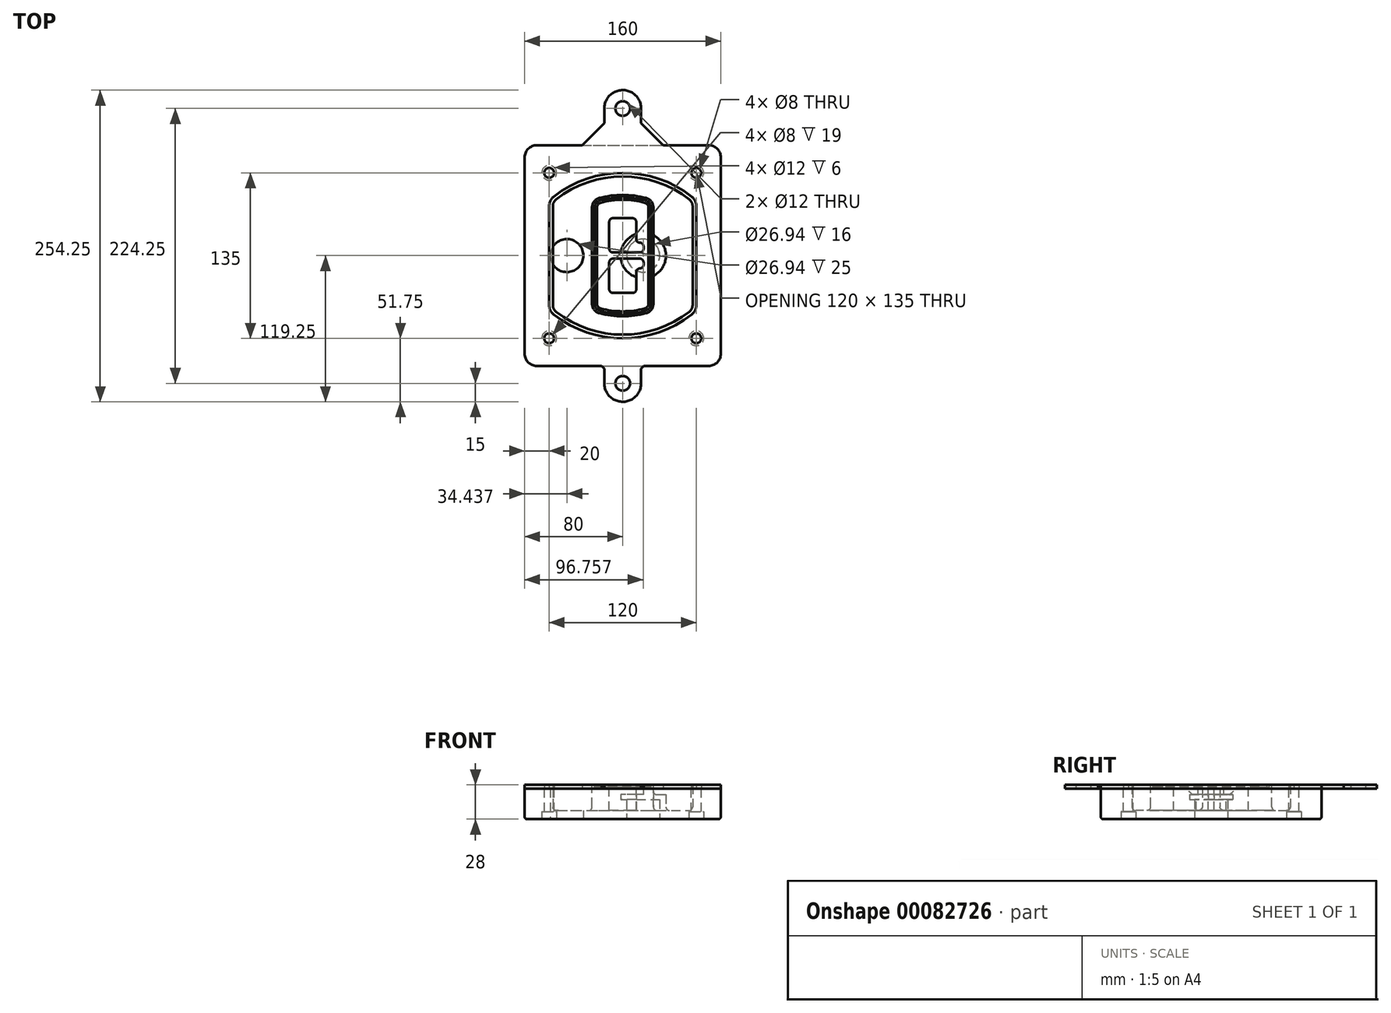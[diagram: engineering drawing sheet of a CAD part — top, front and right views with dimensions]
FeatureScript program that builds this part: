
annotation { "Feature Type Name" : "Feature", "Feature Type Description" : "" }
export const myFeature = defineFeature(function(context is Context, id is Id, definition is map)
    precondition{}
    {
        {
            var Q0;
            Q0=qCreatedBy(makeId("Top.planeOp"),FACE);
            var sketch = newSketch(context, id + "F0", { "sketchPlane" : qUnion([Q0])});
            skPoint(sketch, "E0.rect.middle", {"position": v(0, 0) * mm});
            skLineSegment(sketch, "E1.bottom", {"start": v(-70, -90) * mm, "end": v(70, -90) * mm});
            skLineSegment(sketch, "E1.top", {"start": v(-70, 90) * mm, "end": v(70, 90) * mm});
            skLineSegment(sketch, "E1.left", {"start": v(-80, -80) * mm, "end": v(-80, 80) * mm});
            skLineSegment(sketch, "E1.right", {"start": v(80, -80) * mm, "end": v(80, 80) * mm});
            skLineSegment(sketch, "E2", {"start": v(-80, 90) * mm, "end": v(80, -90) * mm, "construction": true});
            skLineSegment(sketch, "E3", {"start": v(80, 90) * mm, "end": v(-80, -90) * mm, "construction": true});
            skCircle(sketch, "E4", {"center": v(-60, 67.5) * mm, "radius": 4 * mm});
            skCircle(sketch, "E5", {"center": v(60, 67.5) * mm, "radius": 4 * mm});
            skCircle(sketch, "E6", {"center": v(60, -67.5) * mm, "radius": 4 * mm});
            skCircle(sketch, "E7", {"center": v(-60, -67.5) * mm, "radius": 4 * mm});
            skLineSegment(sketch, "E8", {"start": v(-60, 67.5) * mm, "end": v(60, 67.5) * mm, "construction": true});
            skLineSegment(sketch, "E9", {"start": v(60, 67.5) * mm, "end": v(60, -67.5) * mm, "construction": true});
            skLineSegment(sketch, "E10", {"start": v(60, -67.5) * mm, "end": v(-60, -67.5) * mm, "construction": true});
            skLineSegment(sketch, "E11", {"start": v(-60, -67.5) * mm, "end": v(-60, 67.5) * mm, "construction": true});
            skLineSegment(sketch, "E12", {"start": v(-60, 40.3) * mm, "end": v(-60, -40.3) * mm});
            skLineSegment(sketch, "E13", {"start": v(60, 40.3) * mm, "end": v(60, -40.3) * mm});
            skArc(sketch, "E14", {"start": v(56.15, 48.18) * mm, "mid": v(0, 67.5) * mm, "end": v(-56.15, 48.18) * mm});
            skArc(sketch, "E15", {"start": v(-56.15, -48.18) * mm, "mid": v(0, -67.5) * mm, "end": v(56.15, -48.18) * mm});
            skLineSegment(sketch, "E16", {"start": v(-60, 0) * mm, "end": v(60, 0) * mm, "construction": true});
            skPoint(sketch, "E17.visualSharp", {"position": v(-60, -45) * mm});
            skArc(sketch, "E17.filletArc", {"start": v(-60, -40.3) * mm, "mid": v(-58.99, -44.68) * mm, "end": v(-56.15, -48.18) * mm});
            skPoint(sketch, "E18.visualSharp", {"position": v(-60, 45) * mm});
            skArc(sketch, "E18.filletArc", {"start": v(-56.15, 48.18) * mm, "mid": v(-58.99, 44.68) * mm, "end": v(-60, 40.3) * mm});
            skPoint(sketch, "E19.visualSharp", {"position": v(60, 45) * mm});
            skArc(sketch, "E19.filletArc", {"start": v(60, 40.3) * mm, "mid": v(58.99, 44.68) * mm, "end": v(56.15, 48.18) * mm});
            skPoint(sketch, "E20.visualSharp", {"position": v(60, -45) * mm});
            skArc(sketch, "E20.filletArc", {"start": v(56.15, -48.18) * mm, "mid": v(58.99, -44.68) * mm, "end": v(60, -40.3) * mm});
            skPoint(sketch, "E21.visualSharp", {"position": v(-80, 90) * mm});
            skArc(sketch, "E21.filletArc", {"start": v(-70, 90) * mm, "mid": v(-77.07, 87.07) * mm, "end": v(-80, 80) * mm});
            skPoint(sketch, "E22.visualSharp", {"position": v(80, 90) * mm});
            skArc(sketch, "E22.filletArc", {"start": v(80, 80) * mm, "mid": v(77.07, 87.07) * mm, "end": v(70, 90) * mm});
            skPoint(sketch, "E23.visualSharp", {"position": v(80, -90) * mm});
            skArc(sketch, "E23.filletArc", {"start": v(70, -90) * mm, "mid": v(77.07, -87.07) * mm, "end": v(80, -80) * mm});
            skPoint(sketch, "E24.visualSharp", {"position": v(-80, -90) * mm});
            skArc(sketch, "E24.filletArc", {"start": v(-80, -80) * mm, "mid": v(-77.07, -87.07) * mm, "end": v(-70, -90) * mm});
            skArc(sketch, "E25.0", {"start": v(57, 40.3) * mm, "mid": v(56.3, 43.36) * mm, "end": v(54.3, 45.81) * mm});
            skLineSegment(sketch, "E25.1", {"start": v(57, 40.3) * mm, "end": v(57, -40.3) * mm});
            skArc(sketch, "E25.2", {"start": v(54.3, -45.81) * mm, "mid": v(56.3, -43.36) * mm, "end": v(57, -40.3) * mm});
            skArc(sketch, "E25.3", {"start": v(-54.3, -45.81) * mm, "mid": v(0, -64.5) * mm, "end": v(54.3, -45.81) * mm});
            skArc(sketch, "E25.4", {"start": v(-57, -40.3) * mm, "mid": v(-56.3, -43.36) * mm, "end": v(-54.3, -45.81) * mm});
            skArc(sketch, "E25.5", {"start": v(54.3, 45.81) * mm, "mid": v(0, 64.5) * mm, "end": v(-54.3, 45.81) * mm});
            skLineSegment(sketch, "E25.6", {"start": v(-57, 40.3) * mm, "end": v(-57, -40.3) * mm});
            skArc(sketch, "E25.7", {"start": v(-54.3, 45.81) * mm, "mid": v(-56.3, 43.36) * mm, "end": v(-57, 40.3) * mm});
            skArc(sketch, "E26.0", {"start": v(-58.62, 51.33) * mm, "mid": v(-62.58, 46.43) * mm, "end": v(-64, 40.3) * mm});
            skArc(sketch, "E26.1", {"start": v(58.62, 51.33) * mm, "mid": v(0, 71.5) * mm, "end": v(-58.62, 51.33) * mm});
            skArc(sketch, "E26.2", {"start": v(64, 40.3) * mm, "mid": v(62.58, 46.43) * mm, "end": v(58.62, 51.33) * mm});
            skLineSegment(sketch, "E26.3", {"start": v(64, 40.3) * mm, "end": v(64, -40.3) * mm});
            skArc(sketch, "E26.4", {"start": v(58.62, -51.33) * mm, "mid": v(62.58, -46.43) * mm, "end": v(64, -40.3) * mm});
            skLineSegment(sketch, "E26.5", {"start": v(-64, 40.3) * mm, "end": v(-64, -40.3) * mm});
            skArc(sketch, "E26.6", {"start": v(-58.62, -51.33) * mm, "mid": v(0, -71.5) * mm, "end": v(58.62, -51.33) * mm});
            skArc(sketch, "E26.7", {"start": v(-64, -40.3) * mm, "mid": v(-62.58, -46.43) * mm, "end": v(-58.62, -51.33) * mm});
            skSolve(sketch);
        }
        {
            var Q0;
            Q0=makeQuery(id+"F0.imprint","IMPRINT",FACE,{"disambiguationData":[TD([[makeQuery(id+"F0.imprint","IMPRINT",EDGE,{"derivedFrom":sQuery(id+"F0.wireOp",EDGE,"E1.bottom")}),1.0]])]});
            var Q1;
            Q1=makeQuery(id+"F0.imprint","IMPRINT",FACE,{"disambiguationData":[TD([[makeQuery(id+"F0.imprint","IMPRINT",EDGE,{"derivedFrom":sQuery(id+"F0.wireOp",EDGE,"E12")}),1.0]])]});
            var Q2;
            Q2=makeQuery(id+"F0.imprint","IMPRINT",FACE,{"disambiguationData":[TD([[makeQuery(id+"F0.imprint","IMPRINT",EDGE,{"derivedFrom":sQuery(id+"F0.wireOp",EDGE,"E25.0")}),1.0]])]});
            var Q3;
            Q3=makeQuery(id+"F0.imprint","IMPRINT",FACE,{"disambiguationData":[TD([[makeQuery(id+"F0.imprint","IMPRINT",EDGE,{"derivedFrom":sQuery(id+"F0.wireOp",EDGE,"E12")}),-1.0]])]});
            extrude(context, id + "F1", {"entities" : qUnion([Q0, Q1, Q2, Q3]), "oppositeDirection" : true, "depth" : 25 * mm});
        }
        {
            var Q0;
            Q0=makeQuery(id+"F0.imprint","IMPRINT",FACE,{"disambiguationData":[TD([[makeQuery(id+"F0.imprint","IMPRINT",EDGE,{"derivedFrom":sQuery(id+"F0.wireOp",EDGE,"E12")}),1.0]])]});
            extrude(context, id + "F2", {"entities" : qUnion([Q0]), "operationType" : NewBodyOperationType.ADD, "depth" : 3 * mm});
        }
        {
            var Q0;
            Q0=makeQuery(id+"F0.imprint","IMPRINT",FACE,{"disambiguationData":[TD([[makeQuery(id+"F0.imprint","IMPRINT",EDGE,{"derivedFrom":sQuery(id+"F0.wireOp",EDGE,"E25.0")}),1.0]])]});
            extrude(context, id + "F3", {"entities" : qUnion([Q0]), "operationType" : NewBodyOperationType.REMOVE, "oppositeDirection" : true, "depth" : 18 * mm});
        }
        {
            var Q0;
            Q0=makeQuery(id+"F2.opExtrude","CAP_FACE",FACE,{"disambiguationData":[OSD([sQuery(id+"F0.wireOp",EDGE,"E12"),sQuery(id+"F0.wireOp",EDGE,"E13"),sQuery(id+"F0.wireOp",EDGE,"E14"),sQuery(id+"F0.wireOp",EDGE,"E15"),sQuery(id+"F0.wireOp",EDGE,"E17.filletArc"),sQuery(id+"F0.wireOp",EDGE,"E18.filletArc"),sQuery(id+"F0.wireOp",EDGE,"E19.filletArc"),sQuery(id+"F0.wireOp",EDGE,"E20.filletArc"),sQuery(id+"F0.wireOp",EDGE,"E25.0"),sQuery(id+"F0.wireOp",EDGE,"E25.1"),sQuery(id+"F0.wireOp",EDGE,"E25.2"),sQuery(id+"F0.wireOp",EDGE,"E25.3"),sQuery(id+"F0.wireOp",EDGE,"E25.4"),sQuery(id+"F0.wireOp",EDGE,"E25.5"),sQuery(id+"F0.wireOp",EDGE,"E25.6"),sQuery(id+"F0.wireOp",EDGE,"E25.7")])],"isStart":false});
            var sketch = newSketch(context, id + "F4", { "sketchPlane" : qUnion([Q0])});
            skArc(sketch, "E27.0", {"start": v(-19.08, -46.97) * mm, "mid": v(0, -49.5) * mm, "end": v(19.08, -46.97) * mm});
            skArc(sketch, "E28.0", {"start": v(19.08, 46.97) * mm, "mid": v(0, 49.5) * mm, "end": v(-19.08, 46.97) * mm});
            skLineSegment(sketch, "E29", {"start": v(-25, 39.25) * mm, "end": v(-25, -39.25) * mm});
            skLineSegment(sketch, "E30", {"start": v(25, 39.25) * mm, "end": v(25, -39.25) * mm});
            skLineSegment(sketch, "E31", {"start": v(-25, 45.1) * mm, "end": v(25, 45.1) * mm, "construction": true});
            skLineSegment(sketch, "E32", {"start": v(-25, -45.1) * mm, "end": v(25, -45.1) * mm, "construction": true});
            skPoint(sketch, "E33.visualSharp", {"position": v(-25, 45.1) * mm});
            skArc(sketch, "E33.filletArc", {"start": v(-19.08, 46.97) * mm, "mid": v(-23.35, 44.11) * mm, "end": v(-25, 39.25) * mm});
            skPoint(sketch, "E34.visualSharp", {"position": v(25, 45.1) * mm});
            skArc(sketch, "E34.filletArc", {"start": v(25, 39.25) * mm, "mid": v(23.35, 44.11) * mm, "end": v(19.08, 46.97) * mm});
            skPoint(sketch, "E35.visualSharp", {"position": v(25, -45.1) * mm});
            skArc(sketch, "E35.filletArc", {"start": v(19.08, -46.97) * mm, "mid": v(23.35, -44.11) * mm, "end": v(25, -39.25) * mm});
            skPoint(sketch, "E36.visualSharp", {"position": v(-25, -45.1) * mm});
            skArc(sketch, "E36.filletArc", {"start": v(-25, -39.25) * mm, "mid": v(-23.35, -44.11) * mm, "end": v(-19.08, -46.97) * mm});
            skArc(sketch, "E37.0", {"start": v(54.3, 45.81) * mm, "mid": v(0, 64.5) * mm, "end": v(-54.3, 45.81) * mm});
            skArc(sketch, "E37.1", {"start": v(-54.3, 45.81) * mm, "mid": v(-56.3, 43.36) * mm, "end": v(-57, 40.3) * mm});
            skLineSegment(sketch, "E37.2", {"start": v(-57, 40.3) * mm, "end": v(-57, -40.3) * mm});
            skArc(sketch, "E37.3", {"start": v(-57, -40.3) * mm, "mid": v(-56.3, -43.36) * mm, "end": v(-54.3, -45.81) * mm});
            skArc(sketch, "E37.4", {"start": v(-54.3, -45.81) * mm, "mid": v(0, -64.5) * mm, "end": v(54.3, -45.81) * mm});
            skArc(sketch, "E37.5", {"start": v(54.3, -45.81) * mm, "mid": v(56.3, -43.36) * mm, "end": v(57, -40.3) * mm});
            skLineSegment(sketch, "E37.6", {"start": v(57, 40.3) * mm, "end": v(57, -40.3) * mm});
            skArc(sketch, "E37.7", {"start": v(57, 40.3) * mm, "mid": v(56.3, 43.36) * mm, "end": v(54.3, 45.81) * mm});
            skLineSegment(sketch, "E38.0", {"start": v(23, 39.25) * mm, "end": v(23, -39.25) * mm});
            skArc(sketch, "E38.1", {"start": v(18.56, -45.04) * mm, "mid": v(21.76, -42.9) * mm, "end": v(23, -39.25) * mm});
            skArc(sketch, "E38.2", {"start": v(-18.56, -45.04) * mm, "mid": v(0, -47.5) * mm, "end": v(18.56, -45.04) * mm});
            skArc(sketch, "E38.3", {"start": v(-23, -39.25) * mm, "mid": v(-21.76, -42.9) * mm, "end": v(-18.56, -45.04) * mm});
            skLineSegment(sketch, "E38.4", {"start": v(-23, 39.25) * mm, "end": v(-23, -39.25) * mm});
            skArc(sketch, "E38.5", {"start": v(23, 39.25) * mm, "mid": v(21.76, 42.9) * mm, "end": v(18.56, 45.04) * mm});
            skArc(sketch, "E38.6", {"start": v(-18.56, 45.04) * mm, "mid": v(-21.76, 42.9) * mm, "end": v(-23, 39.25) * mm});
            skArc(sketch, "E38.7", {"start": v(18.56, 45.04) * mm, "mid": v(0, 47.5) * mm, "end": v(-18.56, 45.04) * mm});
            skArc(sketch, "E39.0", {"start": v(21, 39.25) * mm, "mid": v(20.18, 41.68) * mm, "end": v(18.04, 43.1) * mm});
            skLineSegment(sketch, "E39.1", {"start": v(21, 39.25) * mm, "end": v(21, -39.25) * mm});
            skArc(sketch, "E39.2", {"start": v(18.04, -43.1) * mm, "mid": v(20.18, -41.68) * mm, "end": v(21, -39.25) * mm});
            skArc(sketch, "E39.3", {"start": v(-18.04, -43.1) * mm, "mid": v(0, -45.5) * mm, "end": v(18.04, -43.1) * mm});
            skArc(sketch, "E39.4", {"start": v(-21, -39.25) * mm, "mid": v(-20.18, -41.68) * mm, "end": v(-18.04, -43.1) * mm});
            skArc(sketch, "E39.5", {"start": v(18.04, 43.1) * mm, "mid": v(0, 45.5) * mm, "end": v(-18.04, 43.1) * mm});
            skLineSegment(sketch, "E39.6", {"start": v(-21, 39.25) * mm, "end": v(-21, -39.25) * mm});
            skArc(sketch, "E39.7", {"start": v(-18.04, 43.1) * mm, "mid": v(-20.18, 41.68) * mm, "end": v(-21, 39.25) * mm});
            skLineSegment(sketch, "E40", {"start": v(-25, 0) * mm, "end": v(25, 0) * mm, "construction": true});
            skLineSegment(sketch, "E41", {"start": v(-11, 5.5) * mm, "end": v(-11, 27.5) * mm});
            skLineSegment(sketch, "E42", {"start": v(-8, 30.5) * mm, "end": v(8, 30.5) * mm});
            skLineSegment(sketch, "E43", {"start": v(11, 27.5) * mm, "end": v(11, 13.5) * mm});
            skLineSegment(sketch, "E44", {"start": v(14, 10.5) * mm, "end": v(14, 10.5) * mm});
            skLineSegment(sketch, "E45", {"start": v(17, 7.5) * mm, "end": v(17, 5.5) * mm});
            skLineSegment(sketch, "E46", {"start": v(14, 2.5) * mm, "end": v(-8, 2.5) * mm});
            skPoint(sketch, "E47.visualSharp", {"position": v(-11, 30.5) * mm});
            skArc(sketch, "E47.filletArc", {"start": v(-8, 30.5) * mm, "mid": v(-10.12, 29.62) * mm, "end": v(-11, 27.5) * mm});
            skPoint(sketch, "E48.visualSharp", {"position": v(11, 30.5) * mm});
            skArc(sketch, "E48.filletArc", {"start": v(11, 27.5) * mm, "mid": v(10.12, 29.62) * mm, "end": v(8, 30.5) * mm});
            skPoint(sketch, "E49.visualSharp", {"position": v(11, 10.5) * mm});
            skArc(sketch, "E49.filletArc", {"start": v(11, 13.5) * mm, "mid": v(11.88, 11.38) * mm, "end": v(14, 10.5) * mm});
            skPoint(sketch, "E50.visualSharp", {"position": v(17, 10.5) * mm});
            skArc(sketch, "E50.filletArc", {"start": v(17, 7.5) * mm, "mid": v(16.12, 9.62) * mm, "end": v(14, 10.5) * mm});
            skPoint(sketch, "E51.visualSharp", {"position": v(17, 2.5) * mm});
            skArc(sketch, "E51.filletArc", {"start": v(14, 2.5) * mm, "mid": v(16.12, 3.38) * mm, "end": v(17, 5.5) * mm});
            skPoint(sketch, "E52.visualSharp", {"position": v(-11, 2.5) * mm});
            skArc(sketch, "E52.filletArc", {"start": v(-11, 5.5) * mm, "mid": v(-10.12, 3.38) * mm, "end": v(-8, 2.5) * mm});
            skLineSegment(sketch, "E53.0.MirrorCS", {"start": v(14, -2.5) * mm, "end": v(-8, -2.5) * mm});
            skArc(sketch, "E54.0.MirrorCS", {"start": v(-11, -5.5) * mm, "mid": v(-10.12, -3.38) * mm, "end": v(-8, -2.5) * mm});
            skLineSegment(sketch, "E55.0.MirrorCS", {"start": v(-11, -5.5) * mm, "end": v(-11, -27.5) * mm});
            skArc(sketch, "E56.0.MirrorCS", {"start": v(-8, -30.5) * mm, "mid": v(-10.12, -29.62) * mm, "end": v(-11, -27.5) * mm});
            skLineSegment(sketch, "E57.0.MirrorCS", {"start": v(-8, -30.5) * mm, "end": v(8, -30.5) * mm});
            skArc(sketch, "E58.0.MirrorCS", {"start": v(11, -27.5) * mm, "mid": v(10.12, -29.62) * mm, "end": v(8, -30.5) * mm});
            skLineSegment(sketch, "E59.0.MirrorCS", {"start": v(11, -27.5) * mm, "end": v(11, -13.5) * mm});
            skArc(sketch, "E60.0.MirrorCS", {"start": v(11, -13.5) * mm, "mid": v(11.88, -11.38) * mm, "end": v(14, -10.5) * mm});
            skArc(sketch, "E61.0.MirrorCS", {"start": v(17, -7.5) * mm, "mid": v(16.12, -9.62) * mm, "end": v(14, -10.5) * mm});
            skLineSegment(sketch, "E62.0.MirrorCS", {"start": v(17, -7.5) * mm, "end": v(17, -5.5) * mm});
            skArc(sketch, "E63.0.MirrorCS", {"start": v(14, -2.5) * mm, "mid": v(16.12, -3.38) * mm, "end": v(17, -5.5) * mm});
            skSolve(sketch);
        }
        {
            var Q0;
            Q0=makeQuery(id+"F4.imprint","IMPRINT",FACE,{"disambiguationData":[TD([[makeQuery(id+"F4.imprint","IMPRINT",EDGE,{"derivedFrom":sQuery(id+"F4.wireOp",EDGE,"E27.0")}),1.0]])]});
            var Q1;
            Q1=makeQuery(id+"F4.imprint","IMPRINT",FACE,{"disambiguationData":[TD([[makeQuery(id+"F4.imprint","IMPRINT",EDGE,{"derivedFrom":sQuery(id+"F4.wireOp",EDGE,"E38.0")}),-1.0]])]});
            var Q2;
            Q2=makeQuery(id+"F4.imprint","IMPRINT",FACE,{"disambiguationData":[TD([[makeQuery(id+"F4.imprint","IMPRINT",EDGE,{"derivedFrom":sQuery(id+"F4.wireOp",EDGE,"E39.0")}),1.0]])]});
            extrude(context, id + "F5", {"entities" : qUnion([Q0, Q1, Q2]), "operationType" : NewBodyOperationType.ADD, "endBound" : BoundingType.UP_TO_NEXT, "oppositeDirection" : true, "depth" : 25 * mm});
        }
        {
            var Q0;
            Q0=makeQuery(id+"F4.imprint","IMPRINT",FACE,{"disambiguationData":[TD([[makeQuery(id+"F4.imprint","IMPRINT",EDGE,{"derivedFrom":sQuery(id+"F4.wireOp",EDGE,"E38.0")}),-1.0]])]});
            extrude(context, id + "F6", {"entities" : qUnion([Q0]), "operationType" : NewBodyOperationType.REMOVE, "oppositeDirection" : true, "depth" : 2 * mm});
        }
        {
            var Q0;
            Q0=makeQuery(id+"F1.opExtrude","CAP_FACE",FACE,{"disambiguationData":[OSD([sQuery(id+"F0.wireOp",EDGE,"E1.bottom"),sQuery(id+"F0.wireOp",EDGE,"E1.top"),sQuery(id+"F0.wireOp",EDGE,"E1.left"),sQuery(id+"F0.wireOp",EDGE,"E1.right"),sQuery(id+"F0.wireOp",EDGE,"E4"),sQuery(id+"F0.wireOp",EDGE,"E5"),sQuery(id+"F0.wireOp",EDGE,"E6"),sQuery(id+"F0.wireOp",EDGE,"E7"),sQuery(id+"F0.wireOp",EDGE,"E21.filletArc"),sQuery(id+"F0.wireOp",EDGE,"E22.filletArc"),sQuery(id+"F0.wireOp",EDGE,"E23.filletArc"),sQuery(id+"F0.wireOp",EDGE,"E24.filletArc")])],"isStart":false});
            var sketch = newSketch(context, id + "F7", { "sketchPlane" : qUnion([Q0])});
            skCircle(sketch, "E64", {"center": v(16.76, 0) * mm, "radius": 13.47 * mm});
            skCircle(sketch, "E65", {"center": v(-45.56, 0) * mm, "radius": 13.47 * mm});
            skLineSegment(sketch, "E66", {"start": v(80, 0) * mm, "end": v(-80, 0) * mm});
            skCircle(sketch, "E67", {"center": v(16.76, 0) * mm, "radius": 18.47 * mm});
            skCircle(sketch, "E68", {"center": v(60, -67.5) * mm, "radius": 6 * mm});
            skCircle(sketch, "E69", {"center": v(-60, -67.5) * mm, "radius": 6 * mm});
            skCircle(sketch, "E70", {"center": v(-60, 67.5) * mm, "radius": 6 * mm});
            skCircle(sketch, "E71", {"center": v(60, 67.5) * mm, "radius": 6 * mm});
            skSolve(sketch);
        }
        {
            var Q0;
            {var subQ1=sQuery(id+"F7.wireOp",EDGE,"E66");var subQ4=sQuery(id+"F7.wireOp",EDGE,"E64");var subQ6=makeQuery(id+"F7.imprint","INTERSECT",VERTEX,{"disambiguationData":[OD(0.0)],"derivedFrom":[subQ4,subQ1]});Q0=makeQuery(id+"F7.imprint","IMPRINT",FACE,{"disambiguationData":[TD([[makeQuery(id+"F7.imprint","IMPRINT",EDGE,{"disambiguationData":[TD([[subQ6,-1.0]])],"derivedFrom":subQ4}),-1.0]])]});}
            var Q1;
            {var subQ0=sQuery(id+"F7.wireOp",EDGE,"E66");var subQ1=sQuery(id+"F7.wireOp",EDGE,"E64");var subQ3=makeQuery(id+"F7.imprint","INTERSECT",VERTEX,{"disambiguationData":[OD(0.0)],"derivedFrom":[subQ1,subQ0]});Q1=makeQuery(id+"F7.imprint","IMPRINT",FACE,{"disambiguationData":[TD([[makeQuery(id+"F7.imprint","IMPRINT",EDGE,{"disambiguationData":[TD([[subQ3,-1.0]])],"derivedFrom":subQ1}),1.0]])]});}
            var Q2;
            {var subQ0=sQuery(id+"F7.wireOp",EDGE,"E66");var subQ1=sQuery(id+"F7.wireOp",EDGE,"E64");var subQ3=makeQuery(id+"F7.imprint","INTERSECT",VERTEX,{"disambiguationData":[OD(0.0)],"derivedFrom":[subQ1,subQ0]});Q2=makeQuery(id+"F7.imprint","IMPRINT",FACE,{"disambiguationData":[TD([[makeQuery(id+"F7.imprint","IMPRINT",EDGE,{"disambiguationData":[TD([[subQ3,1.0]])],"derivedFrom":subQ1}),1.0]])]});}
            var Q3;
            {var subQ1=sQuery(id+"F7.wireOp",EDGE,"E66");var subQ4=sQuery(id+"F7.wireOp",EDGE,"E64");var subQ6=makeQuery(id+"F7.imprint","INTERSECT",VERTEX,{"disambiguationData":[OD(0.0)],"derivedFrom":[subQ4,subQ1]});Q3=makeQuery(id+"F7.imprint","IMPRINT",FACE,{"disambiguationData":[TD([[makeQuery(id+"F7.imprint","IMPRINT",EDGE,{"disambiguationData":[TD([[subQ6,1.0]])],"derivedFrom":subQ4}),-1.0]])]});}
            extrude(context, id + "F8", {"entities" : qUnion([Q0, Q1, Q2, Q3]), "operationType" : NewBodyOperationType.ADD, "oppositeDirection" : true, "depth" : 20 * mm});
        }
        {
            var Q0;
            {var subQ0=sQuery(id+"F7.wireOp",EDGE,"E66");var subQ1=sQuery(id+"F7.wireOp",EDGE,"E64");var subQ3=makeQuery(id+"F7.imprint","INTERSECT",VERTEX,{"disambiguationData":[OD(0.0)],"derivedFrom":[subQ1,subQ0]});Q0=makeQuery(id+"F7.imprint","IMPRINT",FACE,{"disambiguationData":[TD([[makeQuery(id+"F7.imprint","IMPRINT",EDGE,{"disambiguationData":[TD([[subQ3,-1.0]])],"derivedFrom":subQ1}),1.0]])]});}
            var Q1;
            {var subQ0=sQuery(id+"F7.wireOp",EDGE,"E66");var subQ1=sQuery(id+"F7.wireOp",EDGE,"E64");var subQ3=makeQuery(id+"F7.imprint","INTERSECT",VERTEX,{"disambiguationData":[OD(0.0)],"derivedFrom":[subQ1,subQ0]});Q1=makeQuery(id+"F7.imprint","IMPRINT",FACE,{"disambiguationData":[TD([[makeQuery(id+"F7.imprint","IMPRINT",EDGE,{"disambiguationData":[TD([[subQ3,1.0]])],"derivedFrom":subQ1}),1.0]])]});}
            extrude(context, id + "F9", {"entities" : qUnion([Q0, Q1]), "operationType" : NewBodyOperationType.REMOVE, "oppositeDirection" : true, "depth" : 16 * mm});
        }
        {
            var Q0;
            {var subQ0=sQuery(id+"F7.wireOp",EDGE,"E66");var subQ1=sQuery(id+"F7.wireOp",EDGE,"E65");var subQ3=makeQuery(id+"F7.imprint","INTERSECT",VERTEX,{"disambiguationData":[OD(0.0)],"derivedFrom":[subQ1,subQ0]});Q0=makeQuery(id+"F7.imprint","IMPRINT",FACE,{"disambiguationData":[TD([[makeQuery(id+"F7.imprint","IMPRINT",EDGE,{"disambiguationData":[TD([[subQ3,-1.0]])],"derivedFrom":subQ1}),1.0]])]});}
            var Q1;
            {var subQ0=sQuery(id+"F7.wireOp",EDGE,"E66");var subQ1=sQuery(id+"F7.wireOp",EDGE,"E65");var subQ3=makeQuery(id+"F7.imprint","INTERSECT",VERTEX,{"disambiguationData":[OD(0.0)],"derivedFrom":[subQ1,subQ0]});Q1=makeQuery(id+"F7.imprint","IMPRINT",FACE,{"disambiguationData":[TD([[makeQuery(id+"F7.imprint","IMPRINT",EDGE,{"disambiguationData":[TD([[subQ3,1.0]])],"derivedFrom":subQ1}),1.0]])]});}
            extrude(context, id + "F10", {"entities" : qUnion([Q0, Q1]), "operationType" : NewBodyOperationType.REMOVE, "oppositeDirection" : true, "depth" : 25 * mm});
        }
        {
            var Q0;
            Q0=makeQuery(id+"F7.imprint","IMPRINT",FACE,{"disambiguationData":[TD([[makeQuery(id+"F7.imprint","IMPRINT",EDGE,{"derivedFrom":sQuery(id+"F7.wireOp",EDGE,"E68")}),1.0]])]});
            var Q1;
            Q1=makeQuery(id+"F7.imprint","IMPRINT",FACE,{"disambiguationData":[TD([[makeQuery(id+"F7.imprint","IMPRINT",EDGE,{"derivedFrom":makeQuery(id+"F1.opExtrude","CAP_EDGE",EDGE,{"disambiguationData":[OSD([sQuery(id+"F0.wireOp",EDGE,"E5")])],"isStart":false})}),-1.0]])]});
            var Q2;
            Q2=makeQuery(id+"F7.imprint","IMPRINT",FACE,{"disambiguationData":[TD([[makeQuery(id+"F7.imprint","IMPRINT",EDGE,{"derivedFrom":sQuery(id+"F7.wireOp",EDGE,"E69")}),1.0]])]});
            var Q3;
            Q3=makeQuery(id+"F7.imprint","IMPRINT",FACE,{"disambiguationData":[TD([[makeQuery(id+"F7.imprint","IMPRINT",EDGE,{"derivedFrom":makeQuery(id+"F1.opExtrude","CAP_EDGE",EDGE,{"disambiguationData":[OSD([sQuery(id+"F0.wireOp",EDGE,"E4")])],"isStart":false})}),-1.0]])]});
            var Q4;
            Q4=makeQuery(id+"F7.imprint","IMPRINT",FACE,{"disambiguationData":[TD([[makeQuery(id+"F7.imprint","IMPRINT",EDGE,{"derivedFrom":sQuery(id+"F7.wireOp",EDGE,"E70")}),1.0]])]});
            var Q5;
            Q5=makeQuery(id+"F7.imprint","IMPRINT",FACE,{"disambiguationData":[TD([[makeQuery(id+"F7.imprint","IMPRINT",EDGE,{"derivedFrom":makeQuery(id+"F1.opExtrude","CAP_EDGE",EDGE,{"disambiguationData":[OSD([sQuery(id+"F0.wireOp",EDGE,"E7")])],"isStart":false})}),-1.0]])]});
            var Q6;
            Q6=makeQuery(id+"F7.imprint","IMPRINT",FACE,{"disambiguationData":[TD([[makeQuery(id+"F7.imprint","IMPRINT",EDGE,{"derivedFrom":sQuery(id+"F7.wireOp",EDGE,"E71")}),1.0]])]});
            var Q7;
            Q7=makeQuery(id+"F7.imprint","IMPRINT",FACE,{"disambiguationData":[TD([[makeQuery(id+"F7.imprint","IMPRINT",EDGE,{"derivedFrom":makeQuery(id+"F1.opExtrude","CAP_EDGE",EDGE,{"disambiguationData":[OSD([sQuery(id+"F0.wireOp",EDGE,"E6")])],"isStart":false})}),-1.0]])]});
            extrude(context, id + "F11", {"entities" : qUnion([Q0, Q1, Q2, Q3, Q4, Q5, Q6, Q7]), "operationType" : NewBodyOperationType.REMOVE, "oppositeDirection" : true, "depth" : 6 * mm});
        }
        {
            var Q0;
            Q0=makeQuery(id+"F9.boolean.opBoolean","COPY",FACE,{"derivedFrom":makeQuery(id+"F9.opExtrude","CAP_FACE",FACE,{"disambiguationData":[OSD([sQuery(id+"F7.wireOp",EDGE,"E64")])],"isStart":false})});
            var sketch = newSketch(context, id + "F12", { "sketchPlane" : qUnion([Q0])});
            skArc(sketch, "E72.0", {"start": v(11, 17.55) * mm, "mid": v(2.57, 11.82) * mm, "end": v(-1.54, 2.5) * mm});
            skArc(sketch, "E72.1", {"start": v(-1.54, -2.5) * mm, "mid": v(2.57, -11.82) * mm, "end": v(11, -17.55) * mm});
            skLineSegment(sketch, "E73", {"start": v(-1.54, -2.5) * mm, "end": v(14, -2.5) * mm});
            skLineSegment(sketch, "E74.0", {"start": v(14, 2.5) * mm, "end": v(-1.54, 2.5) * mm});
            skArc(sketch, "E74.1", {"start": v(14, 2.5) * mm, "mid": v(16.12, 3.38) * mm, "end": v(17, 5.5) * mm});
            skLineSegment(sketch, "E74.2", {"start": v(17, 7.5) * mm, "end": v(17, 5.5) * mm});
            skArc(sketch, "E74.3", {"start": v(17, 7.5) * mm, "mid": v(16.12, 9.62) * mm, "end": v(14, 10.5) * mm});
            skArc(sketch, "E74.4", {"start": v(11, 13.5) * mm, "mid": v(11.88, 11.38) * mm, "end": v(14, 10.5) * mm});
            skLineSegment(sketch, "E74.5", {"start": v(11, 17.55) * mm, "end": v(11, 13.5) * mm});
            skLineSegment(sketch, "E74.7", {"start": v(14, -2.5) * mm, "end": v(-1.54, -2.5) * mm});
            skArc(sketch, "E74.8", {"start": v(14, -2.5) * mm, "mid": v(16.12, -3.38) * mm, "end": v(17, -5.5) * mm});
            skLineSegment(sketch, "E74.9", {"start": v(17, -7.5) * mm, "end": v(17, -5.5) * mm});
            skArc(sketch, "E74.10", {"start": v(17, -7.5) * mm, "mid": v(16.12, -9.62) * mm, "end": v(14, -10.5) * mm});
            skArc(sketch, "E74.11", {"start": v(11, -13.5) * mm, "mid": v(11.88, -11.38) * mm, "end": v(14, -10.5) * mm});
            skLineSegment(sketch, "E74.12", {"start": v(11, -17.55) * mm, "end": v(11, -13.5) * mm});
            skPoint(sketch, "E75.orphan", {"position": v(11, -27.5) * mm});
            skPoint(sketch, "E76.orphan", {"position": v(-8, -2.5) * mm});
            skPoint(sketch, "E77.orphan", {"position": v(-8, 2.5) * mm});
            skPoint(sketch, "E78.orphan", {"position": v(11, 27.5) * mm});
            skSolve(sketch);
        }
        {
            var Q0;
            {var subQ7=sQuery(id+"F12.wireOp",EDGE,"E72.0");var subQ14=sQuery(id+"F12.wireOp",EDGE,"E72.1");var subQ16=sQuery(id+"F12.wireOp",EDGE,"E74.1");var subQ18=sQuery(id+"F12.wireOp",EDGE,"E74.8");Q0=qUnion([makeQuery(id+"F12.imprint","IMPRINT",FACE,{"disambiguationData":[TD([[makeQuery(id+"F12.imprint","IMPRINT",EDGE,{"derivedFrom":subQ7}),1.0]])]}),makeQuery(id+"F12.imprint","IMPRINT",FACE,{"disambiguationData":[TD([[makeQuery(id+"F12.imprint","IMPRINT",EDGE,{"derivedFrom":subQ14}),1.0]])]}),makeQuery(id+"F12.imprint","IMPRINT",FACE,{"disambiguationData":[TD([[makeQuery(id+"F12.imprint","IMPRINT",EDGE,{"derivedFrom":subQ16}),1.0]])]}),makeQuery(id+"F12.imprint","IMPRINT",FACE,{"disambiguationData":[TD([[makeQuery(id+"F12.imprint","IMPRINT",EDGE,{"derivedFrom":subQ18}),-1.0]])]})]);}
            var Q1;
            Q1=makeQuery(id+"F5.boolean.opBoolean","SPLIT",FACE,{"disambiguationData":[TD([makeQuery(id+"F5.opExtrude","SWEPT_FACE",FACE,{"disambiguationData":[OSD([sQuery(id+"F4.wireOp",EDGE,"E41")])]})])],"derivedFrom":makeQuery(id+"F3.boolean.opBoolean","COPY",FACE,{"derivedFrom":makeQuery(id+"F3.opExtrude","CAP_FACE",FACE,{"disambiguationData":[OSD([sQuery(id+"F0.wireOp",EDGE,"E25.0"),sQuery(id+"F0.wireOp",EDGE,"E25.1"),sQuery(id+"F0.wireOp",EDGE,"E25.2"),sQuery(id+"F0.wireOp",EDGE,"E25.3"),sQuery(id+"F0.wireOp",EDGE,"E25.4"),sQuery(id+"F0.wireOp",EDGE,"E25.5"),sQuery(id+"F0.wireOp",EDGE,"E25.6"),sQuery(id+"F0.wireOp",EDGE,"E25.7")])],"isStart":false})})});
            extrude(context, id + "F13", {"entities" : qUnion([Q0]), "operationType" : NewBodyOperationType.REMOVE, "endBound" : BoundingType.UP_TO_SURFACE, "endBoundEntityFace" : qUnion([Q1]), "depth" : 25 * mm});
        }
        {
            var Q0;
            Q0=makeQuery(id+"F3.boolean.opBoolean","COPY",EDGE,{"derivedFrom":makeQuery(id+"F3.opExtrude","CAP_EDGE",EDGE,{"disambiguationData":[OSD([sQuery(id+"F0.wireOp",EDGE,"E25.6")])],"isStart":false})});
            var Q1;
            Q1=makeQuery(id+"F8.boolean.opBoolean","INTERSECT",EDGE,{"derivedFrom":[makeQuery(id+"F5.opExtrude","SWEPT_FACE",FACE,{"disambiguationData":[OSD([sQuery(id+"F4.wireOp",EDGE,"E30")])]}),makeQuery(id+"F8.opExtrude","CAP_FACE",FACE,{"disambiguationData":[OSD([sQuery(id+"F7.wireOp",EDGE,"E67")])],"isStart":false})]});
            var Q2;
            Q2=makeQuery(id+"F8.boolean.opBoolean","INTERSECT",EDGE,{"disambiguationData":[OD(1.0)],"derivedFrom":[makeQuery(id+"F5.opExtrude","SWEPT_FACE",FACE,{"disambiguationData":[OSD([sQuery(id+"F4.wireOp",EDGE,"E30")])]}),makeQuery(id+"F8.opExtrude","SWEPT_FACE",FACE,{"disambiguationData":[OSD([sQuery(id+"F7.wireOp",EDGE,"E67")])]})]});
            var Q3;
            {var subQ0=sQuery(id+"F4.wireOp",EDGE,"E30");Q3=makeQuery(id+"F8.boolean.opBoolean","SPLIT",EDGE,{"disambiguationData":[TD([makeQuery(id+"F5.opExtrude","SWEPT_FACE",FACE,{"disambiguationData":[OSD([sQuery(id+"F4.wireOp",EDGE,"E35.filletArc")])]})])],"derivedFrom":makeQuery(id+"F5.opExtrude","CAP_EDGE",EDGE,{"disambiguationData":[OSD([subQ0])],"isStart":false})});}
            var Q4;
            {var subQ0=sQuery(id+"F0.wireOp",EDGE,"E25.7");var subQ1=sQuery(id+"F0.wireOp",EDGE,"E25.1");var subQ2=sQuery(id+"F0.wireOp",EDGE,"E25.6");var subQ3=sQuery(id+"F0.wireOp",EDGE,"E25.5");var subQ4=sQuery(id+"F0.wireOp",EDGE,"E25.4");var subQ5=sQuery(id+"F0.wireOp",EDGE,"E25.0");var subQ6=sQuery(id+"F0.wireOp",EDGE,"E25.2");var subQ7=sQuery(id+"F0.wireOp",EDGE,"E25.3");Q4=makeQuery(id+"F8.boolean.opBoolean","INTERSECT",EDGE,{"derivedFrom":[makeQuery(id+"F5.boolean.opBoolean","SPLIT",FACE,{"disambiguationData":[TD([makeQuery(id+"F2.opExtrude","SWEPT_FACE",FACE,{"disambiguationData":[OSD([subQ5])]})])],"derivedFrom":makeQuery(id+"F3.boolean.opBoolean","COPY",FACE,{"derivedFrom":makeQuery(id+"F3.opExtrude","CAP_FACE",FACE,{"disambiguationData":[OSD([subQ5,subQ1,subQ6,subQ7,subQ4,subQ3,subQ2,subQ0])],"isStart":false})})}),makeQuery(id+"F8.opExtrude","SWEPT_FACE",FACE,{"disambiguationData":[OSD([sQuery(id+"F7.wireOp",EDGE,"E67")])]})]});}
            var Q5;
            Q5=makeQuery(id+"F8.boolean.opBoolean","INTERSECT",EDGE,{"disambiguationData":[OD(0.0)],"derivedFrom":[makeQuery(id+"F5.opExtrude","SWEPT_FACE",FACE,{"disambiguationData":[OSD([sQuery(id+"F4.wireOp",EDGE,"E30")])]}),makeQuery(id+"F8.opExtrude","SWEPT_FACE",FACE,{"disambiguationData":[OSD([sQuery(id+"F7.wireOp",EDGE,"E67")])]})]});
            fillet(context, id + "F14", {"entities" : qUnion([Q0, Q1, Q2, Q3, Q4, Q5]), "radius" : 3 * mm, "tangentPropagation" : true, "allowEdgeOverflow" : false});
        }
        {
            var Q0;
            Q0=makeQuery(id+"F1.opExtrude","CAP_EDGE",EDGE,{"disambiguationData":[OSD([sQuery(id+"F0.wireOp",EDGE,"E1.bottom")])],"isStart":false});
            fillet(context, id + "F15", {"entities" : qUnion([Q0]), "radius" : 2 * mm, "tangentPropagation" : true, "allowEdgeOverflow" : false});
        }
        {
            var Q0;
            {var subQ0=sQuery(id+"F0.wireOp",EDGE,"E22.filletArc");var subQ1=sQuery(id+"F0.wireOp",EDGE,"E7");var subQ2=sQuery(id+"F0.wireOp",EDGE,"E6");var subQ3=sQuery(id+"F0.wireOp",EDGE,"E5");var subQ4=sQuery(id+"F0.wireOp",EDGE,"E4");var subQ5=sQuery(id+"F0.wireOp",EDGE,"E1.bottom");var subQ6=sQuery(id+"F0.wireOp",EDGE,"E21.filletArc");var subQ7=sQuery(id+"F0.wireOp",EDGE,"E1.top");var subQ8=sQuery(id+"F0.wireOp",EDGE,"E1.left");var subQ9=sQuery(id+"F0.wireOp",EDGE,"E1.right");var subQ10=sQuery(id+"F0.wireOp",EDGE,"E23.filletArc");var subQ11=sQuery(id+"F0.wireOp",EDGE,"E24.filletArc");Q0=makeQuery(id+"F2.boolean.opBoolean","SPLIT",FACE,{"disambiguationData":[TD([makeQuery(id+"F1.opExtrude","SWEPT_FACE",FACE,{"disambiguationData":[OSD([subQ5])]})])],"derivedFrom":makeQuery(id+"F1.opExtrude","CAP_FACE",FACE,{"disambiguationData":[OSD([subQ5,subQ7,subQ8,subQ9,subQ4,subQ3,subQ2,subQ1,subQ6,subQ0,subQ10,subQ11])],"isStart":true})});}
            var sketch = newSketch(context, id + "F16", { "sketchPlane" : qUnion([Q0])});
            skLineSegment(sketch, "E79", {"start": v(-33, 90) * mm, "end": v(-15, 108) * mm});
            skLineSegment(sketch, "E80", {"start": v(-15, 108) * mm, "end": v(-15, 119.94) * mm});
            skCircle(sketch, "E81", {"center": v(0, 120) * mm, "radius": 6 * mm});
            skLineSegment(sketch, "E82", {"start": v(15, 108) * mm, "end": v(33, 90) * mm});
            skLineSegment(sketch, "E83", {"start": v(15, 120) * mm, "end": v(15, 108) * mm});
            skArc(sketch, "E84", {"start": v(15, 120) * mm, "mid": v(-0.03, 135) * mm, "end": v(-15, 119.94) * mm});
            skLineSegment(sketch, "E85.MirrorCS", {"start": v(15, -92.25) * mm, "end": v(33, -74.25) * mm});
            skLineSegment(sketch, "E86.MirrorCS", {"start": v(-33, -74.25) * mm, "end": v(-15, -92.25) * mm});
            skLineSegment(sketch, "E87.MirrorCS", {"start": v(15, -104.25) * mm, "end": v(15, -92.25) * mm});
            skLineSegment(sketch, "E88.MirrorCS", {"start": v(-15, -92.25) * mm, "end": v(-15, -104.19) * mm});
            skArc(sketch, "E89.MirrorCS", {"start": v(15, -104.25) * mm, "mid": v(-0.03, -119.25) * mm, "end": v(-15, -104.19) * mm});
            skCircle(sketch, "E90.MirrorC", {"center": v(0, -104.25) * mm, "radius": 6 * mm});
            skSolve(sketch);
        }
        {
            var Q0;
            {var subQ1=sQuery(id+"F16.wireOp",EDGE,"E79");Q0=makeQuery(id+"F16.imprint","IMPRINT",FACE,{"disambiguationData":[TD([[makeQuery(id+"F16.imprint","IMPRINT",EDGE,{"derivedFrom":subQ1}),-1.0]])]});}
            var Q1;
            Q1=makeQuery(id+"F16.imprint","IMPRINT",FACE,{"disambiguationData":[TD([[makeQuery(id+"F16.imprint","IMPRINT",EDGE,{"derivedFrom":makeQuery(id+"F1.opExtrude","CAP_EDGE",EDGE,{"disambiguationData":[OSD([sQuery(id+"F0.wireOp",EDGE,"E1.left")])],"isStart":true})}),-1.0]])]});
            var Q2;
            {var subQ0=sQuery(id+"F16.wireOp",EDGE,"E85.MirrorCS");Q2=makeQuery(id+"F16.imprint","IMPRINT",FACE,{"disambiguationData":[TD([[makeQuery(id+"F16.imprint","IMPRINT",EDGE,{"derivedFrom":subQ0}),1.0]])]});}
            var Q3;
            Q3=makeQuery(id+"F2.opExtrude","CAP_FACE",FACE,{"disambiguationData":[OSD([sQuery(id+"F0.wireOp",EDGE,"E12"),sQuery(id+"F0.wireOp",EDGE,"E13"),sQuery(id+"F0.wireOp",EDGE,"E14"),sQuery(id+"F0.wireOp",EDGE,"E15"),sQuery(id+"F0.wireOp",EDGE,"E17.filletArc"),sQuery(id+"F0.wireOp",EDGE,"E18.filletArc"),sQuery(id+"F0.wireOp",EDGE,"E19.filletArc"),sQuery(id+"F0.wireOp",EDGE,"E20.filletArc"),sQuery(id+"F0.wireOp",EDGE,"E25.0"),sQuery(id+"F0.wireOp",EDGE,"E25.1"),sQuery(id+"F0.wireOp",EDGE,"E25.2"),sQuery(id+"F0.wireOp",EDGE,"E25.3"),sQuery(id+"F0.wireOp",EDGE,"E25.4"),sQuery(id+"F0.wireOp",EDGE,"E25.5"),sQuery(id+"F0.wireOp",EDGE,"E25.6"),sQuery(id+"F0.wireOp",EDGE,"E25.7")])],"isStart":false});
            extrude(context, id + "F17", {"entities" : qUnion([Q0, Q1, Q2]), "endBound" : BoundingType.UP_TO_SURFACE, "endBoundEntityFace" : qUnion([Q3]), "depth" : 25 * mm});
        }
    });
